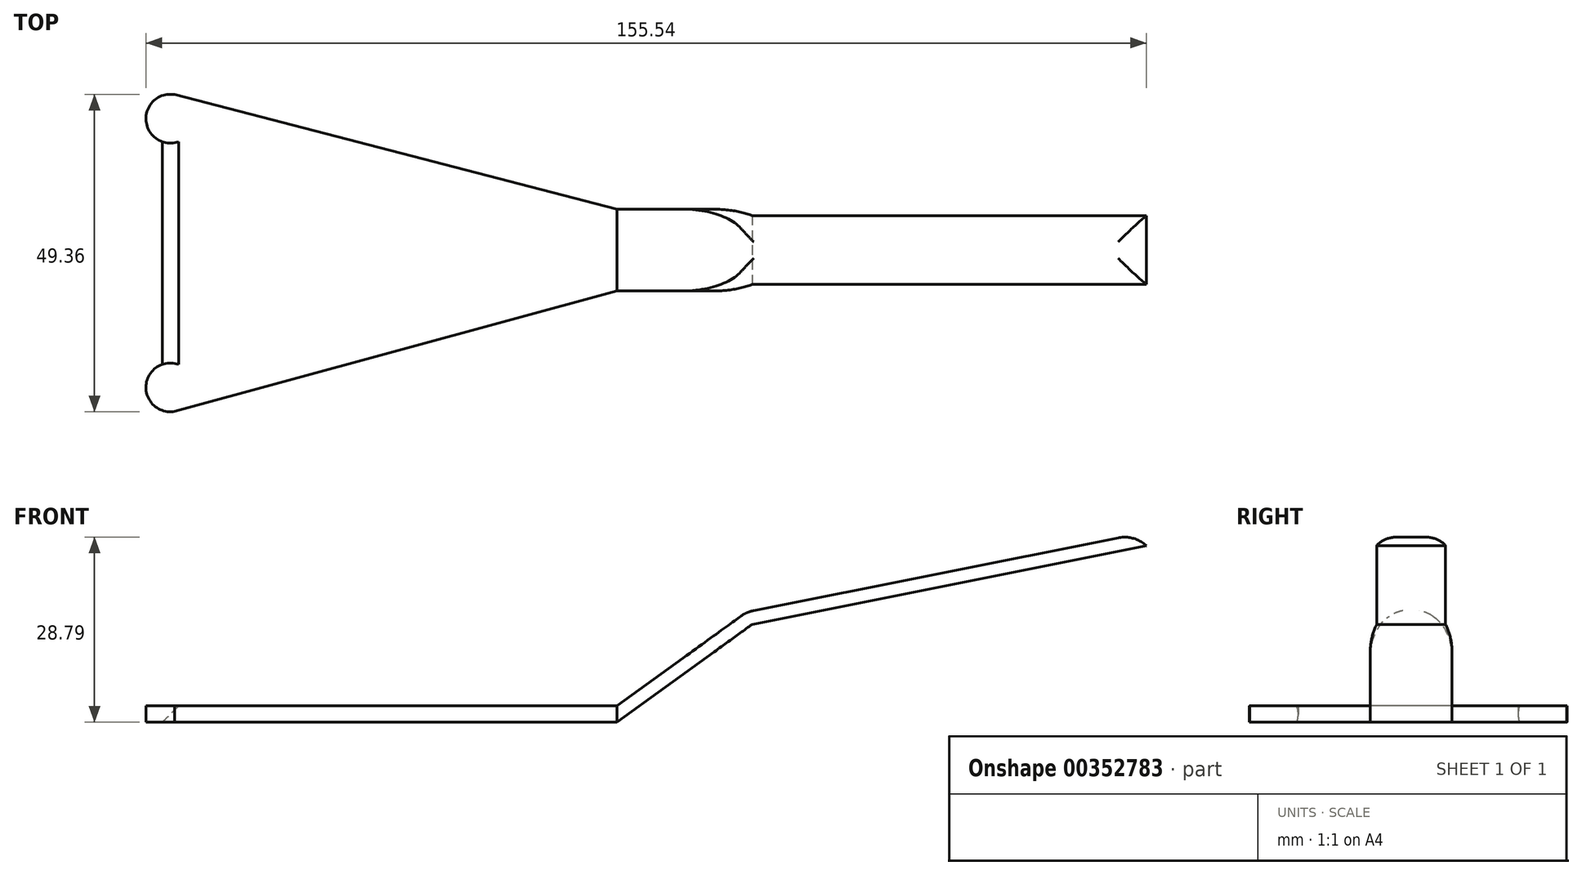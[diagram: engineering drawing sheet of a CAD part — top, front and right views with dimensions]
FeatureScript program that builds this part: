
annotation { "Feature Type Name" : "Feature", "Feature Type Description" : "" }
export const myFeature = defineFeature(function(context is Context, id is Id, definition is map)
    precondition{}
    {
        {
            var Q0;
            Q0=qCreatedBy(makeId("Top.planeOp"),FACE);
            var sketch = newSketch(context, id + "F0", { "sketchPlane" : qUnion([Q0])});
            skLineSegment(sketch, "E0", {"start": v(-73.24, -0.5) * mm, "end": v(-73.24, 20.4) * mm});
            skLineSegment(sketch, "E1", {"start": v(-73.24, -0.5) * mm, "end": v(-73.24, -21.34) * mm});
            skLineSegment(sketch, "E2", {"start": v(0, 0) * mm, "end": v(0, -6.35) * mm});
            skLineSegment(sketch, "E3", {"start": v(0, -6.35) * mm, "end": v(0, 0) * mm});
            skPoint(sketch, "E4.visualSharp", {"position": v(-73.24, 24.9) * mm});
            skArc(sketch, "E4.filletArc", {"start": v(-68.8, 24.17) * mm, "mid": v(-71.9, 23.32) * mm, "end": v(-73.24, 20.4) * mm});
            skPoint(sketch, "E5.visualSharp", {"position": v(-73.24, -25.9) * mm});
            skArc(sketch, "E5.filletArc", {"start": v(-73.24, -21.34) * mm, "mid": v(-71.88, -24.26) * mm, "end": v(-68.76, -25.08) * mm});
            skLineSegment(sketch, "E6", {"start": v(0, 0) * mm, "end": v(0, 6.35) * mm});
            skLineSegment(sketch, "E7", {"start": v(-68.8, 24.17) * mm, "end": v(0, 6.35) * mm});
            skLineSegment(sketch, "E8", {"start": v(-68.76, -25.08) * mm, "end": v(0, -6.35) * mm});
            skSolve(sketch);
        }
        {
            var Q0;
            Q0=makeQuery(id+"F0.imprint","IMPRINT",FACE,{"disambiguationData":[TD([[makeQuery(id+"F0.imprint","IMPRINT",EDGE,{"derivedFrom":sQuery(id+"F0.wireOp",EDGE,"E0")}),-1.0]])]});
            extrude(context, id + "F1", {"entities" : qUnion([Q0]), "endBound" : BoundingType.SYMMETRIC, "depth" : 2.54 * mm});
        }
        {
            var Q0;
            Q0=qCreatedBy(makeId("Front.planeOp"),FACE);
            var sketch = newSketch(context, id + "F2", { "sketchPlane" : qUnion([Q0])});
            skLineSegment(sketch, "E9", {"start": v(0, 0) * mm, "end": v(20.56, 14.92) * mm});
            skLineSegment(sketch, "E10", {"start": v(20.56, 14.92) * mm, "end": v(82.83, 27.36) * mm});
            skSolve(sketch);
        }
        {
            var Q0;
            Q0=makeQuery(id+"F1.opExtrude","SWEPT_FACE",FACE,{"disambiguationData":[OSD([sQuery(id+"F0.wireOp",EDGE,"E3"),sQuery(id+"F0.wireOp",EDGE,"E6")])]});
            var Q1;
            Q1=sQuery(id+"F2.wireOp",EDGE,"E9");
            var Q2;
            Q2=sQuery(id+"F2.wireOp",EDGE,"E10");
            sweep(context, id + "F3", {"operationType" : NewBodyOperationType.ADD, "profiles" : qUnion([Q0]), "path" : qUnion([Q1, Q2])});
        }
        {
            var Q0;
            {var subQ0=sQuery(id+"F2.wireOp",EDGE,"E10");var subQ1=sQuery(id+"F0.wireOp",EDGE,"E6");var subQ2=sQuery(id+"F0.wireOp",EDGE,"E3");Q0=makeQuery(id+"F3.opSweep","SWEPT_FACE",FACE,{"disambiguationData":[OSD([subQ2,subQ1,subQ0]),TDD([makeQuery(id+"F1.opExtrude","CAP_EDGE",EDGE,{"disambiguationData":[OSD([subQ2,subQ1])],"isStart":false}),subQ0])]});}
            fillet(context, id + "F4", {"entities" : qUnion([Q0]), "radius" : 5.08 * mm, "tangentPropagation" : true, "allowEdgeOverflow" : false});
        }
        {
            var Q0;
            Q0=makeQuery(id+"F1.opExtrude","CAP_EDGE",EDGE,{"disambiguationData":[OSD([sQuery(id+"F0.wireOp",EDGE,"E0"),sQuery(id+"F0.wireOp",EDGE,"E1")])],"isStart":false});
            chamfer(context, id + "F5", {"entities" : qUnion([Q0]), "width" : 5.08 * mm, "tangentPropagation" : true});
        }
    });
